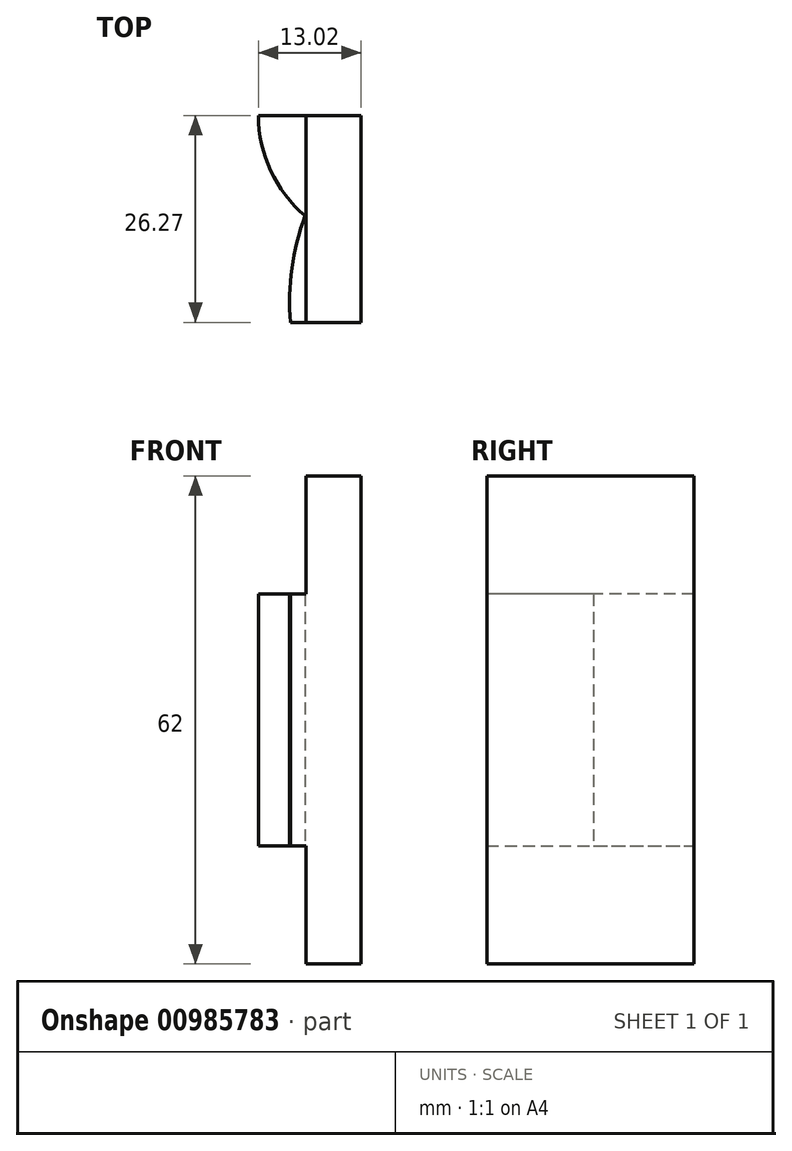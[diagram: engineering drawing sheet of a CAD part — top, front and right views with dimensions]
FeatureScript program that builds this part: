
annotation { "Feature Type Name" : "Feature", "Feature Type Description" : "" }
export const myFeature = defineFeature(function(context is Context, id is Id, definition is map)
    precondition{}
    {
        {
            var Q0;
            Q0=qCreatedBy(makeId("Top.planeOp"),FACE);
            var sketch = newSketch(context, id + "F0", { "sketchPlane" : qUnion([Q0])});
            skLineSegment(sketch, "E0", {"start": v(87.2, -51.86) * mm, "end": v(87.2, -64.47) * mm});
            skArc(sketch, "E1", {"start": v(87.2, -64.47) * mm, "mid": v(88.75, -71.49) * mm, "end": v(93.12, -77.2) * mm});
            skArc(sketch, "E2", {"start": v(93.12, -77.2) * mm, "mid": v(91.45, -83.87) * mm, "end": v(91.25, -90.74) * mm});
            skLineSegment(sketch, "E3", {"start": v(87.2, -64.47) * mm, "end": v(100.22, -64.47) * mm});
            skLineSegment(sketch, "E4", {"start": v(100.22, -64.47) * mm, "end": v(100.22, -90.74) * mm});
            skLineSegment(sketch, "E5", {"start": v(100.22, -90.74) * mm, "end": v(91.25, -90.74) * mm});
            skPoint(sketch, "E6", {"position": v(68.12, -77.2) * mm});
            skSolve(sketch);
        }
        {
            var Q0;
            Q0=makeQuery(id+"F0.imprint","IMPRINT",FACE,{"disambiguationData":[TD([[makeQuery(id+"F0.imprint","IMPRINT",EDGE,{"derivedFrom":sQuery(id+"F0.wireOp",EDGE,"E1")}),1.0]])]});
            extrude(context, id + "F1", {"entities" : qUnion([Q0]), "depth" : 62 * mm, "offsetDistance" : 25 * mm});
        }
        {
            var Q0;
            Q0=makeQuery(id+"F1.opExtrude","SWEPT_FACE",FACE,{"disambiguationData":[OSD([sQuery(id+"F0.wireOp",EDGE,"E4")])]});
            cPlane(context, id + "F2", {"entities" : qUnion([Q0]), "cplaneType" : CPlaneType.OFFSET, "offset" : 7 * mm, "oppositeDirection" : true, "width" : 150 * mm, "height" : 150 * mm});
        }
        {
            var Q0;
            Q0=qCreatedBy(id+"F2.planeOp",FACE);
            var sketch = newSketch(context, id + "F3", { "sketchPlane" : qUnion([Q0])});
            skLineSegment(sketch, "E7.bottom", {"start": v(-64.47, 62) * mm, "end": v(-90.74, 62) * mm});
            skLineSegment(sketch, "E7.top", {"start": v(-64.47, 47) * mm, "end": v(-90.74, 47) * mm});
            skLineSegment(sketch, "E7.left", {"start": v(-64.47, 62) * mm, "end": v(-64.47, 47) * mm});
            skLineSegment(sketch, "E7.right", {"start": v(-90.74, 62) * mm, "end": v(-90.74, 47) * mm});
            skLineSegment(sketch, "E8.bottom", {"start": v(-90.74, 0) * mm, "end": v(-64.47, 0) * mm});
            skLineSegment(sketch, "E8.top", {"start": v(-90.74, 15) * mm, "end": v(-64.47, 15) * mm});
            skLineSegment(sketch, "E8.left", {"start": v(-90.74, 0) * mm, "end": v(-90.74, 15) * mm});
            skLineSegment(sketch, "E8.right", {"start": v(-64.47, 0) * mm, "end": v(-64.47, 15) * mm});
            skSolve(sketch);
        }
        {
            var Q0;
            Q0 = qSketchRegion(id + "F3", true);
            extrude(context, id + "F4", {"entities" : qUnion([Q0]), "operationType" : NewBodyOperationType.REMOVE, "oppositeDirection" : true, "depth" : 25 * mm, "offsetDistance" : 25 * mm});
        }
    });
